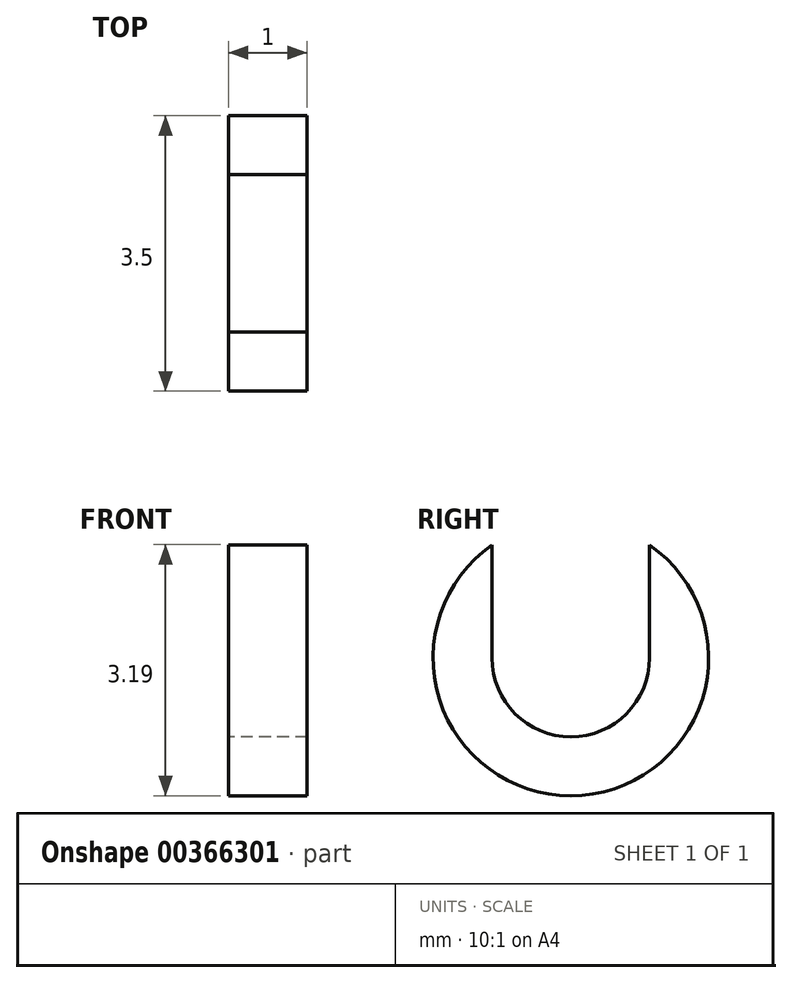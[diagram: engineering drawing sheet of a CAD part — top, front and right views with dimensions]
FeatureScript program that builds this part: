
annotation { "Feature Type Name" : "Feature", "Feature Type Description" : "" }
export const myFeature = defineFeature(function(context is Context, id is Id, definition is map)
    precondition{}
    {
        {
            var Q0;
            Q0=qCreatedBy(makeId("Right.planeOp"),FACE);
            var sketch = newSketch(context, id + "F0", { "sketchPlane" : qUnion([Q0])});
            skArc(sketch, "E0", {"start": v(-1, 1.44) * mm, "mid": v(0, -1.75) * mm, "end": v(1, 1.44) * mm});
            skArc(sketch, "E1", {"start": v(-1, 0) * mm, "mid": v(0, -1) * mm, "end": v(1, 0) * mm});
            skLineSegment(sketch, "E2", {"start": v(1, 0) * mm, "end": v(1, 1.44) * mm});
            skLineSegment(sketch, "E3", {"start": v(-1, 0) * mm, "end": v(-1, 1.44) * mm});
            skSolve(sketch);
        }
        {
            var Q0;
            Q0 = qSketchRegion(id + "F0", true);
            extrude(context, id + "F1", {"entities" : qUnion([Q0]), "depth" : 1 * mm});
        }
    });
